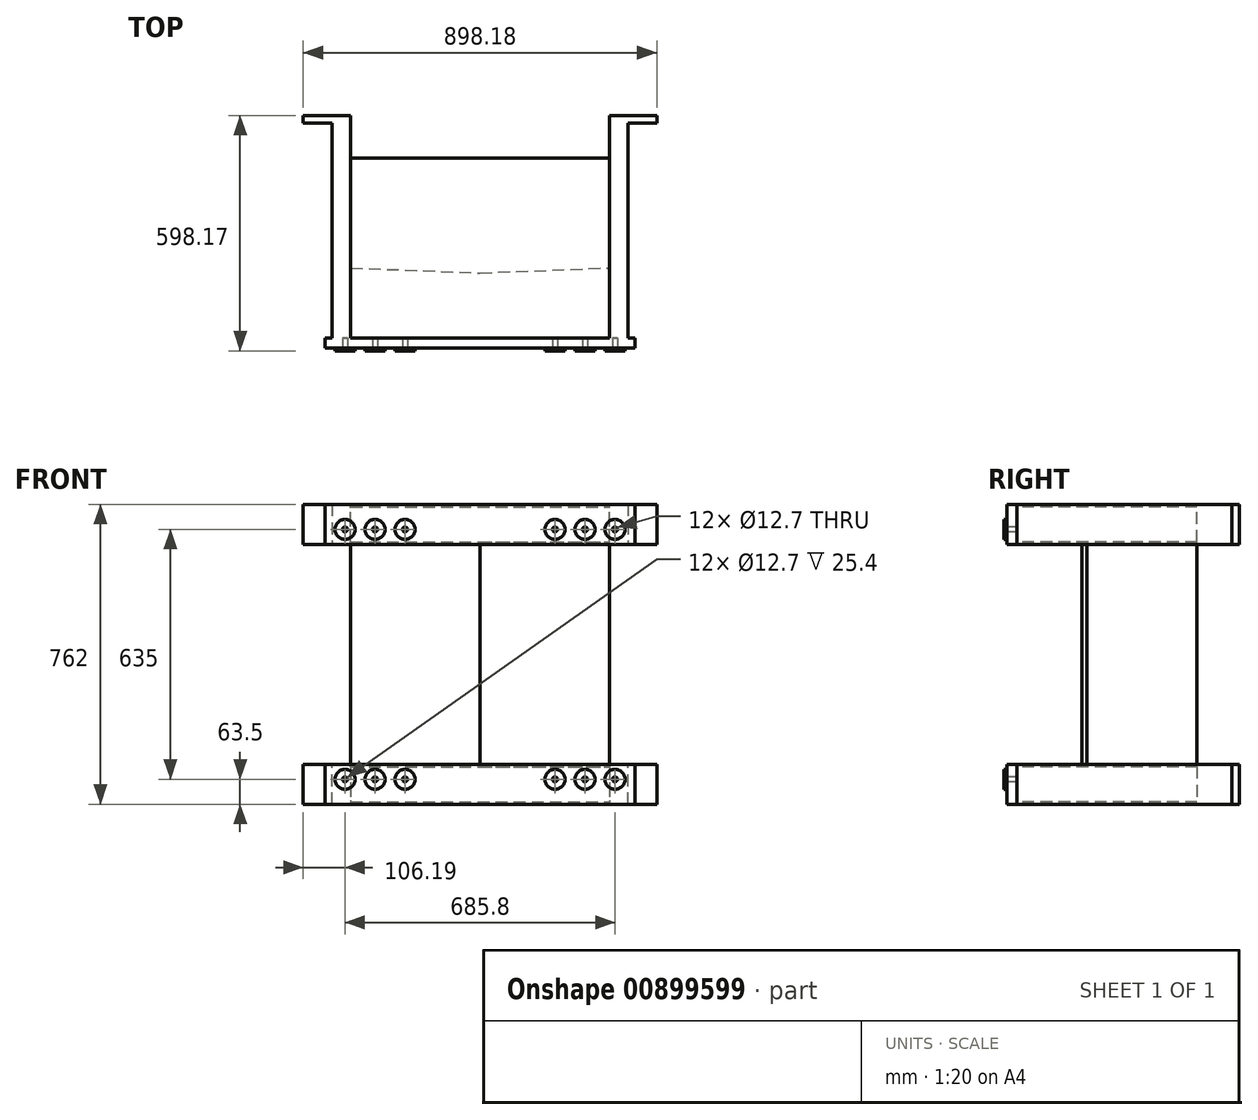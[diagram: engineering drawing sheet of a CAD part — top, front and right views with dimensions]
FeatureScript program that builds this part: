
annotation { "Feature Type Name" : "Feature", "Feature Type Description" : "" }
export const myFeature = defineFeature(function(context is Context, id is Id, definition is map)
    precondition{}
    {
        {
            var Q0;
            Q0=qCreatedBy(makeId("Front.planeOp"),FACE);
            var sketch = newSketch(context, id + "F0", { "sketchPlane" : qUnion([Q0])});
            skLineSegment(sketch, "E0.bottom", {"start": v(393.7, -50.8) * mm, "end": v(-393.7, -50.8) * mm});
            skLineSegment(sketch, "E0.top", {"start": v(393.7, 50.8) * mm, "end": v(-393.7, 50.8) * mm});
            skLineSegment(sketch, "E0.left", {"start": v(393.7, -50.8) * mm, "end": v(393.7, 50.8) * mm});
            skLineSegment(sketch, "E0.right", {"start": v(-393.7, -50.8) * mm, "end": v(-393.7, 50.8) * mm});
            skPoint(sketch, "E0.middle", {"position": v(0, 0) * mm});
            skSolve(sketch);
        }
        {
            var Q0;
            Q0 = qSketchRegion(id + "F0", true);
            extrude(context, id + "F1", {"entities" : qUnion([Q0]), "depth" : 25.4 * mm, "offsetDistance" : 25.4 * mm});
        }
        {
            var Q0;
            Q0=makeQuery(id+"F1.opExtrude","CAP_FACE",FACE,{"disambiguationData":[OSD([sQuery(id+"F0.wireOp",EDGE,"E0.bottom"),sQuery(id+"F0.wireOp",EDGE,"E0.top"),sQuery(id+"F0.wireOp",EDGE,"E0.left"),sQuery(id+"F0.wireOp",EDGE,"E0.right")])],"isStart":true});
            var sketch = newSketch(context, id + "F2", { "sketchPlane" : qUnion([Q0])});
            skLineSegment(sketch, "E1.bottom", {"start": v(368.3, -44.45) * mm, "end": v(-368.3, -44.45) * mm});
            skLineSegment(sketch, "E1.top", {"start": v(368.3, 44.45) * mm, "end": v(-368.3, 44.45) * mm});
            skLineSegment(sketch, "E1.left", {"start": v(368.3, -44.45) * mm, "end": v(368.3, 44.45) * mm});
            skLineSegment(sketch, "E1.right", {"start": v(-368.3, -44.45) * mm, "end": v(-368.3, 44.45) * mm});
            skPoint(sketch, "E1.middle", {"position": v(0, 0) * mm});
            skSolve(sketch);
        }
        {
            var Q0;
            Q0 = qSketchRegion(id + "F2", true);
            extrude(context, id + "F3", {"entities" : qUnion([Q0]), "operationType" : NewBodyOperationType.ADD, "depth" : 457.2 * mm, "offsetDistance" : 25.4 * mm});
        }
        {
            var Q0;
            Q0=makeQuery(id+"F1.opExtrude","CAP_FACE",FACE,{"disambiguationData":[OSD([sQuery(id+"F0.wireOp",EDGE,"E0.bottom"),sQuery(id+"F0.wireOp",EDGE,"E0.top"),sQuery(id+"F0.wireOp",EDGE,"E0.left"),sQuery(id+"F0.wireOp",EDGE,"E0.right")])],"isStart":true});
            var sketch = newSketch(context, id + "F4", { "sketchPlane" : qUnion([Q0])});
            skLineSegment(sketch, "E2", {"start": v(328.44, -44.45) * mm, "end": v(328.44, -50.8) * mm});
            skLineSegment(sketch, "E3", {"start": v(328.44, -50.8) * mm, "end": v(375.66, -50.8) * mm});
            skLineSegment(sketch, "E4", {"start": v(375.66, -50.8) * mm, "end": v(375.66, 50.8) * mm});
            skLineSegment(sketch, "E5", {"start": v(375.66, 50.8) * mm, "end": v(328.44, 50.8) * mm});
            skLineSegment(sketch, "E6", {"start": v(328.44, 50.8) * mm, "end": v(328.44, 44.45) * mm});
            skLineSegment(sketch, "E7", {"start": v(328.44, 44.45) * mm, "end": v(368.3, 44.45) * mm});
            skLineSegment(sketch, "E8", {"start": v(368.3, 44.45) * mm, "end": v(368.3, -44.45) * mm});
            skLineSegment(sketch, "E9", {"start": v(368.3, -44.45) * mm, "end": v(328.44, -44.45) * mm});
            skLineSegment(sketch, "E10.MirrorCS", {"start": v(-328.44, -50.8) * mm, "end": v(-375.66, -50.8) * mm});
            skLineSegment(sketch, "E11.MirrorCS", {"start": v(-368.3, -44.45) * mm, "end": v(-328.44, -44.45) * mm});
            skLineSegment(sketch, "E12.MirrorCS", {"start": v(-328.44, -44.45) * mm, "end": v(-328.44, -50.8) * mm});
            skLineSegment(sketch, "E13.MirrorCS", {"start": v(-375.66, -50.8) * mm, "end": v(-375.66, 50.8) * mm});
            skLineSegment(sketch, "E14.MirrorCS", {"start": v(-368.3, 44.45) * mm, "end": v(-368.3, -44.45) * mm});
            skLineSegment(sketch, "E15.MirrorCS", {"start": v(-328.44, 50.8) * mm, "end": v(-328.44, 44.45) * mm});
            skLineSegment(sketch, "E16.MirrorCS", {"start": v(-328.44, 44.45) * mm, "end": v(-368.3, 44.45) * mm});
            skLineSegment(sketch, "E17.MirrorCS", {"start": v(-375.66, 50.8) * mm, "end": v(-328.44, 50.8) * mm});
            skSolve(sketch);
        }
        {
            var Q0;
            Q0 = qSketchRegion(id + "F4", true);
            extrude(context, id + "F5", {"entities" : qUnion([Q0]), "operationType" : NewBodyOperationType.ADD, "depth" : 546.1 * mm, "offsetDistance" : 25.4 * mm});
        }
        {
            var Q0;
            Q0=makeQuery(id+"F3.opExtrude","CAP_FACE",FACE,{"disambiguationData":[OSD([sQuery(id+"F2.wireOp",EDGE,"E1.bottom"),sQuery(id+"F2.wireOp",EDGE,"E1.top"),sQuery(id+"F2.wireOp",EDGE,"E1.left"),sQuery(id+"F2.wireOp",EDGE,"E1.right")])],"isStart":false});
            var sketch = newSketch(context, id + "F6", { "sketchPlane" : qUnion([Q0])});
            skLineSegment(sketch, "E18.bottom", {"start": v(-328.44, 44.45) * mm, "end": v(-368.3, 44.45) * mm});
            skLineSegment(sketch, "E18.top", {"start": v(-328.44, -44.45) * mm, "end": v(-368.3, -44.45) * mm});
            skLineSegment(sketch, "E18.left", {"start": v(-328.44, 44.45) * mm, "end": v(-328.44, -44.45) * mm});
            skLineSegment(sketch, "E18.right", {"start": v(-368.3, 44.45) * mm, "end": v(-368.3, -44.45) * mm});
            skLineSegment(sketch, "E19.MirrorCS", {"start": v(328.44, 44.45) * mm, "end": v(328.44, -44.45) * mm});
            skLineSegment(sketch, "E20.MirrorCS", {"start": v(328.44, 44.45) * mm, "end": v(368.3, 44.45) * mm});
            skLineSegment(sketch, "E21.MirrorCS", {"start": v(368.3, 44.45) * mm, "end": v(368.3, -44.45) * mm});
            skLineSegment(sketch, "E22.MirrorCS", {"start": v(328.44, -44.45) * mm, "end": v(368.3, -44.45) * mm});
            skSolve(sketch);
        }
        {
            var Q0;
            Q0 = qSketchRegion(id + "F6", true);
            var Q1;
            Q1=makeQuery(id+"F5.opExtrude","CAP_FACE",FACE,{"disambiguationData":[OSD([sQuery(id+"F4.wireOp",EDGE,"E10.MirrorCS"),sQuery(id+"F4.wireOp",EDGE,"E11.MirrorCS"),sQuery(id+"F4.wireOp",EDGE,"E12.MirrorCS"),sQuery(id+"F4.wireOp",EDGE,"E13.MirrorCS"),sQuery(id+"F4.wireOp",EDGE,"E14.MirrorCS"),sQuery(id+"F4.wireOp",EDGE,"E15.MirrorCS"),sQuery(id+"F4.wireOp",EDGE,"E16.MirrorCS"),sQuery(id+"F4.wireOp",EDGE,"E17.MirrorCS")])],"isStart":false});
            extrude(context, id + "F7", {"entities" : qUnion([Q0]), "operationType" : NewBodyOperationType.ADD, "endBound" : BoundingType.UP_TO_SURFACE, "depth" : 25.4 * mm, "endBoundEntityFace" : qUnion([Q1]), "offsetDistance" : 25.4 * mm});
        }
        {
            var Q0;
            Q0=makeQuery(id+"F7.boolean.opBoolean","MERGE",FACE,{"derivedFrom":[makeQuery(id+"F5.opExtrude","CAP_FACE",FACE,{"disambiguationData":[OSD([sQuery(id+"F4.wireOp",EDGE,"E10.MirrorCS"),sQuery(id+"F4.wireOp",EDGE,"E11.MirrorCS"),sQuery(id+"F4.wireOp",EDGE,"E12.MirrorCS"),sQuery(id+"F4.wireOp",EDGE,"E13.MirrorCS"),sQuery(id+"F4.wireOp",EDGE,"E14.MirrorCS"),sQuery(id+"F4.wireOp",EDGE,"E15.MirrorCS"),sQuery(id+"F4.wireOp",EDGE,"E16.MirrorCS"),sQuery(id+"F4.wireOp",EDGE,"E17.MirrorCS")])],"isStart":false}),makeQuery(id+"F7.opExtrude","CAP_FACE",FACE,{"disambiguationData":[OSD([sQuery(id+"F6.wireOp",EDGE,"E18.bottom"),sQuery(id+"F6.wireOp",EDGE,"E18.top"),sQuery(id+"F6.wireOp",EDGE,"E18.left"),sQuery(id+"F6.wireOp",EDGE,"E18.right")])],"isStart":false})]});
            var sketch = newSketch(context, id + "F8", { "sketchPlane" : qUnion([Q0])});
            skLineSegment(sketch, "E23.bottom", {"start": v(-328.44, 50.8) * mm, "end": v(-449.1, 50.8) * mm});
            skLineSegment(sketch, "E23.top", {"start": v(-328.44, -50.8) * mm, "end": v(-449.1, -50.8) * mm});
            skLineSegment(sketch, "E23.left", {"start": v(-328.44, 50.8) * mm, "end": v(-328.44, -50.8) * mm});
            skLineSegment(sketch, "E23.right", {"start": v(-449.1, 50.8) * mm, "end": v(-449.1, -50.8) * mm});
            skLineSegment(sketch, "E24.MirrorCS", {"start": v(328.44, 50.8) * mm, "end": v(328.44, -50.8) * mm});
            skLineSegment(sketch, "E25.MirrorCS", {"start": v(328.44, 50.8) * mm, "end": v(449.1, 50.8) * mm});
            skLineSegment(sketch, "E26.MirrorCS", {"start": v(449.1, 50.8) * mm, "end": v(449.1, -50.8) * mm});
            skLineSegment(sketch, "E27.MirrorCS", {"start": v(328.44, -50.8) * mm, "end": v(449.1, -50.8) * mm});
            skSolve(sketch);
        }
        {
            var Q0;
            Q0 = qSketchRegion(id + "F8", true);
            extrude(context, id + "F9", {"entities" : qUnion([Q0]), "operationType" : NewBodyOperationType.ADD, "depth" : 19.05 * mm, "offsetDistance" : 25.4 * mm});
        }
        {
            var Q0;
            Q0=qCreatedBy(makeId("Top.planeOp"),FACE);
            cPlane(context, id + "F10", {"entities" : qUnion([Q0]), "cplaneType" : CPlaneType.OFFSET, "offset" : 330.2 * mm, "width" : 152.4 * mm, "height" : 152.4 * mm});
        }
        {
            var Q0;
            Q0=makeQuery(id+"F1.opExtrude","SWEPT_BODY",BODY,{"disambiguationData":[OSD([sQuery(id+"F0.wireOp",EDGE,"E0.bottom"),sQuery(id+"F0.wireOp",EDGE,"E0.top"),sQuery(id+"F0.wireOp",EDGE,"E0.left"),sQuery(id+"F0.wireOp",EDGE,"E0.right")])]});
            var Q1;
            Q1=qCreatedBy(id+"F10.planeOp",FACE);
            mirror(context, id + "F11", {"entities" : qUnion([Q0]), "mirrorPlane" : qUnion([Q1])});
        }
        {
            var Q0;
            Q0=makeQuery(id+"F11.opPattern","COPY",FACE,{"derivedFrom":makeQuery(id+"F3.opExtrude","SWEPT_FACE",FACE,{"disambiguationData":[OSD([sQuery(id+"F2.wireOp",EDGE,"E1.top")])]}),"instanceName":"1"});
            var sketch = newSketch(context, id + "F12", { "sketchPlane" : qUnion([Q0])});
            skLineSegment(sketch, "E28.bottom", {"start": v(-328.44, -457.2) * mm, "end": v(328.44, -457.2) * mm});
            skLineSegment(sketch, "E28.left", {"start": v(-328.44, -457.2) * mm, "end": v(-328.44, -177.8) * mm});
            skLineSegment(sketch, "E28.right", {"start": v(328.44, -457.2) * mm, "end": v(328.44, -177.8) * mm});
            skLineSegment(sketch, "E29", {"start": v(0, -177.8) * mm, "end": v(0, 0) * mm, "construction": true});
            skLineSegment(sketch, "E30", {"start": v(-328.44, -177.8) * mm, "end": v(0, -165.1) * mm});
            skLineSegment(sketch, "E31", {"start": v(0, -165.1) * mm, "end": v(328.44, -177.8) * mm});
            skSolve(sketch);
        }
        {
            var Q0;
            Q0 = qSketchRegion(id + "F12", true);
            var Q1;
            Q1=makeQuery(id+"F3.opExtrude","SWEPT_FACE",FACE,{"disambiguationData":[OSD([sQuery(id+"F2.wireOp",EDGE,"E1.top")])]});
            extrude(context, id + "F13", {"entities" : qUnion([Q0]), "endBound" : BoundingType.UP_TO_SURFACE, "depth" : 25.4 * mm, "endBoundEntityFace" : qUnion([Q1]), "offsetDistance" : 25.4 * mm});
        }
        {
            var Q0;
            Q0=makeQuery(id+"F1.opExtrude","CAP_FACE",FACE,{"disambiguationData":[OSD([sQuery(id+"F0.wireOp",EDGE,"E0.bottom"),sQuery(id+"F0.wireOp",EDGE,"E0.top"),sQuery(id+"F0.wireOp",EDGE,"E0.left"),sQuery(id+"F0.wireOp",EDGE,"E0.right")])],"isStart":false});
            var sketch = newSketch(context, id + "F14", { "sketchPlane" : qUnion([Q0])});
            skLineSegment(sketch, "E32", {"start": v(0, -79.13) * mm, "end": v(0, 730.38) * mm, "construction": true});
            skCircle(sketch, "E33", {"center": v(190.5, 12.7) * mm, "radius": 6.35 * mm});
            skCircle(sketch, "E34", {"center": v(266.7, 12.7) * mm, "radius": 6.35 * mm});
            skCircle(sketch, "E35", {"center": v(342.9, 12.7) * mm, "radius": 6.35 * mm});
            skCircle(sketch, "E36.MirrorC", {"center": v(190.5, 647.7) * mm, "radius": 6.35 * mm});
            skCircle(sketch, "E37.MirrorC", {"center": v(266.7, 647.7) * mm, "radius": 6.35 * mm});
            skCircle(sketch, "E38.MirrorC", {"center": v(342.9, 647.7) * mm, "radius": 6.35 * mm});
            skCircle(sketch, "E39.MirrorC", {"center": v(-190.5, 647.7) * mm, "radius": 6.35 * mm});
            skCircle(sketch, "E40.MirrorC", {"center": v(-266.7, 647.7) * mm, "radius": 6.35 * mm});
            skCircle(sketch, "E41.MirrorC", {"center": v(-342.9, 647.7) * mm, "radius": 6.35 * mm});
            skCircle(sketch, "E42.MirrorC", {"center": v(-190.5, 12.7) * mm, "radius": 6.35 * mm});
            skCircle(sketch, "E43.MirrorC", {"center": v(-266.7, 12.7) * mm, "radius": 6.35 * mm});
            skCircle(sketch, "E44.MirrorC", {"center": v(-342.9, 12.7) * mm, "radius": 6.35 * mm});
            skSolve(sketch);
        }
        {
            var Q0;
            Q0 = qSketchRegion(id + "F14", true);
            extrude(context, id + "F15", {"entities" : qUnion([Q0]), "operationType" : NewBodyOperationType.REMOVE, "oppositeDirection" : true, "depth" : 25.4 * mm, "offsetDistance" : 25.4 * mm});
        }
        {
            var Q0;
            Q0=makeQuery(id+"F1.opExtrude","CAP_FACE",FACE,{"disambiguationData":[OSD([sQuery(id+"F0.wireOp",EDGE,"E0.bottom"),sQuery(id+"F0.wireOp",EDGE,"E0.top"),sQuery(id+"F0.wireOp",EDGE,"E0.left"),sQuery(id+"F0.wireOp",EDGE,"E0.right")])],"isStart":false});
            var sketch = newSketch(context, id + "F16", { "sketchPlane" : qUnion([Q0])});
            skCircle(sketch, "E45", {"center": v(190.5, 12.7) * mm, "radius": 25.4 * mm});
            skCircle(sketch, "E46", {"center": v(190.5, 12.7) * mm, "radius": 6.35 * mm});
            skCircle(sketch, "E47", {"center": v(266.7, 12.7) * mm, "radius": 25.4 * mm});
            skCircle(sketch, "E48", {"center": v(342.9, 12.7) * mm, "radius": 25.4 * mm});
            skCircle(sketch, "E49", {"center": v(266.7, 12.7) * mm, "radius": 6.35 * mm});
            skCircle(sketch, "E50", {"center": v(342.9, 12.7) * mm, "radius": 6.35 * mm});
            skLineSegment(sketch, "E51", {"start": v(0, 715.14) * mm, "end": v(0, -60.84) * mm, "construction": true});
            skCircle(sketch, "E52.MirrorC", {"center": v(190.5, 647.7) * mm, "radius": 25.4 * mm});
            skCircle(sketch, "E53.MirrorC", {"center": v(190.5, 647.7) * mm, "radius": 6.35 * mm});
            skCircle(sketch, "E54.MirrorC", {"center": v(266.7, 647.7) * mm, "radius": 6.35 * mm});
            skCircle(sketch, "E55.MirrorC", {"center": v(266.7, 647.7) * mm, "radius": 25.4 * mm});
            skCircle(sketch, "E56.MirrorC", {"center": v(342.9, 647.7) * mm, "radius": 25.4 * mm});
            skCircle(sketch, "E57.MirrorC", {"center": v(342.9, 647.7) * mm, "radius": 6.35 * mm});
            skCircle(sketch, "E58.MirrorC", {"center": v(-190.5, 647.7) * mm, "radius": 25.4 * mm});
            skCircle(sketch, "E59.MirrorC", {"center": v(-190.5, 647.7) * mm, "radius": 6.35 * mm});
            skCircle(sketch, "E60.MirrorC", {"center": v(-266.7, 647.7) * mm, "radius": 6.35 * mm});
            skCircle(sketch, "E61.MirrorC", {"center": v(-266.7, 647.7) * mm, "radius": 25.4 * mm});
            skCircle(sketch, "E62.MirrorC", {"center": v(-342.9, 647.7) * mm, "radius": 25.4 * mm});
            skCircle(sketch, "E63.MirrorC", {"center": v(-342.9, 647.7) * mm, "radius": 6.35 * mm});
            skCircle(sketch, "E64.MirrorC", {"center": v(-190.5, 12.7) * mm, "radius": 6.35 * mm});
            skCircle(sketch, "E65.MirrorC", {"center": v(-190.5, 12.7) * mm, "radius": 25.4 * mm});
            skCircle(sketch, "E66.MirrorC", {"center": v(-266.7, 12.7) * mm, "radius": 25.4 * mm});
            skCircle(sketch, "E67.MirrorC", {"center": v(-266.7, 12.7) * mm, "radius": 6.35 * mm});
            skCircle(sketch, "E68.MirrorC", {"center": v(-342.9, 12.7) * mm, "radius": 25.4 * mm});
            skCircle(sketch, "E69.MirrorC", {"center": v(-342.9, 12.7) * mm, "radius": 6.35 * mm});
            skSolve(sketch);
        }
        {
            var Q0;
            Q0 = qSketchRegion(id + "F16", true);
            extrude(context, id + "F17", {"entities" : qUnion([Q0]), "depth" : 7.62 * mm, "offsetDistance" : 25.4 * mm});
        }
    });
